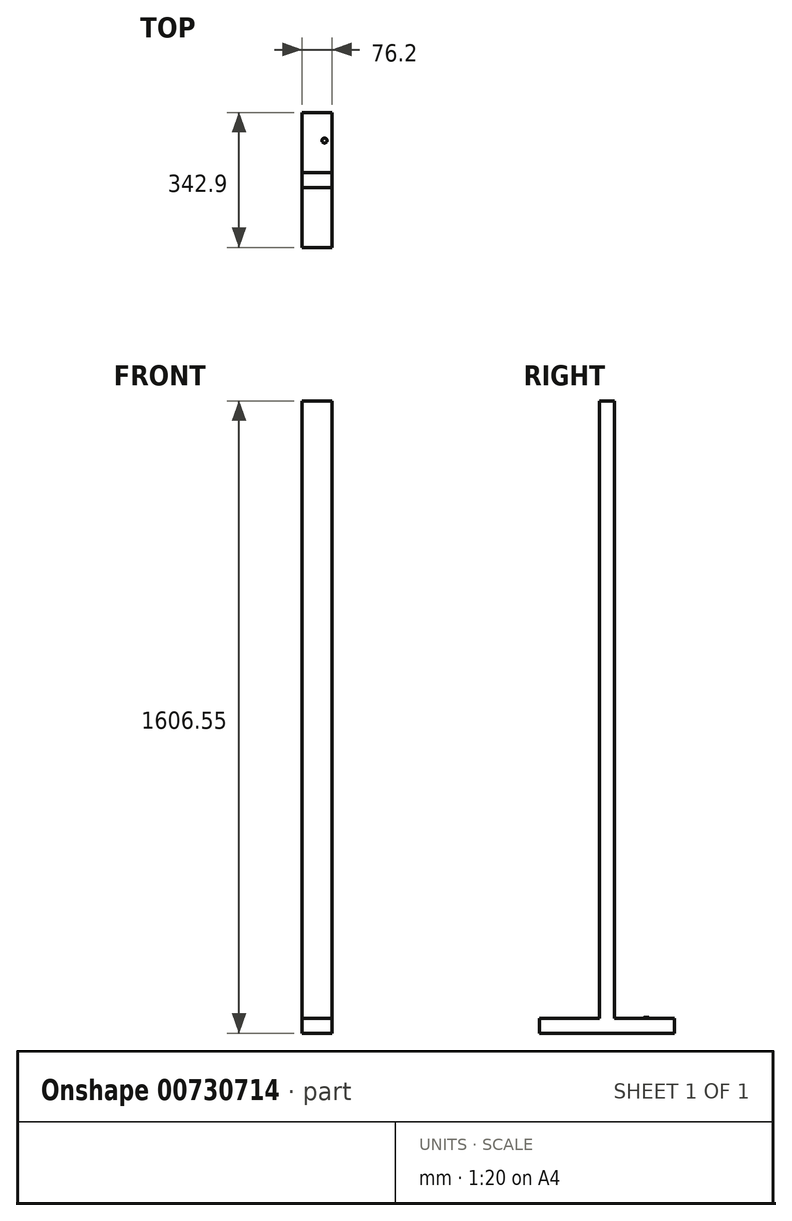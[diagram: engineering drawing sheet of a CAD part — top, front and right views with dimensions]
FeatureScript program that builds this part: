
annotation { "Feature Type Name" : "Feature", "Feature Type Description" : "" }
export const myFeature = defineFeature(function(context is Context, id is Id, definition is map)
    precondition{}
    {
        {
            var Q0;
            Q0=qCreatedBy(makeId("Top.planeOp"),FACE);
            var sketch = newSketch(context, id + "F0", { "sketchPlane" : qUnion([Q0])});
            skLineSegment(sketch, "E0.bottom", {"start": v(38.1, -19.05) * mm, "end": v(-38.1, -19.05) * mm});
            skLineSegment(sketch, "E0.top", {"start": v(38.1, 19.05) * mm, "end": v(-38.1, 19.05) * mm});
            skLineSegment(sketch, "E0.left", {"start": v(38.1, -19.05) * mm, "end": v(38.1, 19.05) * mm});
            skLineSegment(sketch, "E0.right", {"start": v(-38.1, -19.05) * mm, "end": v(-38.1, 19.05) * mm});
            skPoint(sketch, "E0.middle", {"position": v(0, 0) * mm});
            skSolve(sketch);
        }
        {
            var Q0;
            Q0=makeQuery(id+"F0.imprint","IMPRINT",FACE,{"disambiguationData":[TD([[makeQuery(id+"F0.imprint","IMPRINT",EDGE,{"derivedFrom":sQuery(id+"F0.wireOp",EDGE,"E0.bottom")}),-1.0]])]});
            extrude(context, id + "F1", {"entities" : qUnion([Q0]), "depth" : 1568.45 * mm, "offsetDistance" : 25.4 * mm});
        }
        {
            var Q0;
            Q0=makeQuery(id+"F1.opExtrude","CAP_FACE",FACE,{"disambiguationData":[OSD([sQuery(id+"F0.wireOp",EDGE,"E0.bottom"),sQuery(id+"F0.wireOp",EDGE,"E0.top"),sQuery(id+"F0.wireOp",EDGE,"E0.left"),sQuery(id+"F0.wireOp",EDGE,"E0.right")])],"isStart":true});
            var sketch = newSketch(context, id + "F2", { "sketchPlane" : qUnion([Q0])});
            skLineSegment(sketch, "E1.bottom", {"start": v(38.1, -19.05) * mm, "end": v(-38.1, -19.05) * mm});
            skLineSegment(sketch, "E1.top", {"start": v(38.1, 19.05) * mm, "end": v(-38.1, 19.05) * mm});
            skLineSegment(sketch, "E1.left", {"start": v(38.1, -19.05) * mm, "end": v(38.1, 19.05) * mm});
            skLineSegment(sketch, "E1.right", {"start": v(-38.1, -19.05) * mm, "end": v(-38.1, 19.05) * mm});
            skSolve(sketch);
        }
        {
            var Q0;
            Q0=makeQuery(id+"F2.imprint","IMPRINT",FACE,{"disambiguationData":[TD([[makeQuery(id+"F2.imprint","IMPRINT",EDGE,{"derivedFrom":sQuery(id+"F2.wireOp",EDGE,"E1.bottom")}),-1.0]])]});
            extrude(context, id + "F3", {"entities" : qUnion([Q0]), "operationType" : NewBodyOperationType.ADD, "depth" : 38.1 * mm, "offsetDistance" : 25.4 * mm});
        }
        {
            var Q0;
            Q0=makeQuery(id+"F3.boolean.opBoolean","MERGE",FACE,{"derivedFrom":[makeQuery(id+"F1.opExtrude","SWEPT_FACE",FACE,{"disambiguationData":[OSD([sQuery(id+"F0.wireOp",EDGE,"E0.bottom")])]}),makeQuery(id+"F3.opExtrude","SWEPT_FACE",FACE,{"disambiguationData":[OSD([sQuery(id+"F2.wireOp",EDGE,"E1.top")])]})]});
            var sketch = newSketch(context, id + "F4", { "sketchPlane" : qUnion([Q0])});
            skLineSegment(sketch, "E2.bottom", {"start": v(38.1, 0) * mm, "end": v(-38.1, 0) * mm});
            skLineSegment(sketch, "E2.top", {"start": v(38.1, -38.1) * mm, "end": v(-38.1, -38.1) * mm});
            skLineSegment(sketch, "E2.left", {"start": v(38.1, 0) * mm, "end": v(38.1, -38.1) * mm});
            skLineSegment(sketch, "E2.right", {"start": v(-38.1, 0) * mm, "end": v(-38.1, -38.1) * mm});
            skSolve(sketch);
        }
        {
            var Q0;
            Q0 = qSketchRegion(id + "F4", true);
            extrude(context, id + "F5", {"entities" : qUnion([Q0]), "operationType" : NewBodyOperationType.ADD, "depth" : 152.4 * mm, "offsetDistance" : 25.4 * mm, "hasSecondDirection" : true, "secondDirectionOppositeDirection" : true, "secondDirectionDepth" : 190.5 * mm});
        }
        {
            var Q0;
            {var subQ2=sQuery(id+"F4.wireOp",EDGE,"E2.bottom");Q0=makeQuery(id+"F5.boolean.opBoolean","SPLIT",FACE,{"disambiguationData":[TD([makeQuery(id+"F1.opExtrude","SWEPT_FACE",FACE,{"disambiguationData":[OSD([sQuery(id+"F0.wireOp",EDGE,"E0.top")])]})])],"derivedFrom":makeQuery(id+"F5.opExtrude","SWEPT_FACE",FACE,{"disambiguationData":[OSD([subQ2])]})});}
            var sketch = newSketch(context, id + "F6", { "sketchPlane" : qUnion([Q0])});
            skLineSegment(sketch, "E3.bottom", {"start": v(38.1, 126.8) * mm, "end": v(0, 126.8) * mm});
            skLineSegment(sketch, "E3.top", {"start": v(38.1, 72.93) * mm, "end": v(0, 72.93) * mm});
            skLineSegment(sketch, "E3.left", {"start": v(38.1, 126.8) * mm, "end": v(38.1, 72.93) * mm});
            skLineSegment(sketch, "E3.right", {"start": v(0, 126.8) * mm, "end": v(0, 72.93) * mm});
            skCircle(sketch, "E4", {"center": v(19.05, 99.87) * mm, "radius": 6.35 * mm});
            skPoint(sketch, "E4.centerSnap0", {"position": v(19.05, 126.8) * mm});
            skPoint(sketch, "E4.centerSnap1", {"position": v(0, 99.87) * mm});
            skSolve(sketch);
        }
        {
            var Q0;
            Q0=makeQuery(id+"F6.imprint","IMPRINT",FACE,{"disambiguationData":[TD([[makeQuery(id+"F6.imprint","IMPRINT",EDGE,{"derivedFrom":sQuery(id+"F6.wireOp",EDGE,"E4")}),1.0]])]});
            extrude(context, id + "F7", {"entities" : qUnion([Q0]), "operationType" : NewBodyOperationType.ADD, "depth" : 2.54 * mm, "offsetDistance" : 25.4 * mm});
        }
    });
